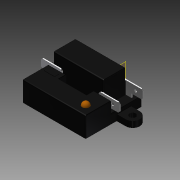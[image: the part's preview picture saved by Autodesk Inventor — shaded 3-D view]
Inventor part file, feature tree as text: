
AUTODESK INVENTOR PART (.ipt)
format: ipt  version: 2013 (Build 170138000, 138)  size: 404,992 bytes
history: native  units: mm (DEFAULTED — no unit token found)
features: sketch x3, fillet x2, plane x2, extrude x2, other x1, hole x1, mirror x1, imported_body x1
ambient origin geometry x8: Origin, YZ Plane, XZ Plane, XY Plane, X Axis, Y Axis, Z Axis, Center Point
bodies: Solid1 (feature_tree)
feature tree (13):
  other  "Spike Relay.ipt"
  fillet  "Fillet1"  Radius=0.762mm
  sketch  "Sketch2"  dims[d14=13.208mm d15=29.083mm]
  plane  "Work Plane1"
  extrude  "Extrusion1"  Depth=29.083mm
  extrude  "Extrusion2"  Depth=25.4mm TaperAngle=0.0deg
  hole  "Hole1"  [1 undecoded]
  plane  "Work Plane2"
  mirror  "Mirror2"
  fillet  "Fillet2"  [1 undecoded]
  imported_body  "DerivedBody::Spike Relay.ipt"
  sketch  "Sketch3"  dims[d16=34.0868mm d17=-4.318mm d18=25.4mm d19=0.0mm]
  sketch  "Sketch4"  dims[d20=25.4mm d21=0.0mm d22=4.4958mm d23=19.05mm d24=8.4328mm d25=6.35mm d26=14.3117mm d27=25.4mm d28=20.594885mm d29=0.635mm]
note: 2 required parameter values undecoded (feature->parameter linkage not recoverable at this tier; creation-order binding heuristic only, values carry confidence <= 0.55)
